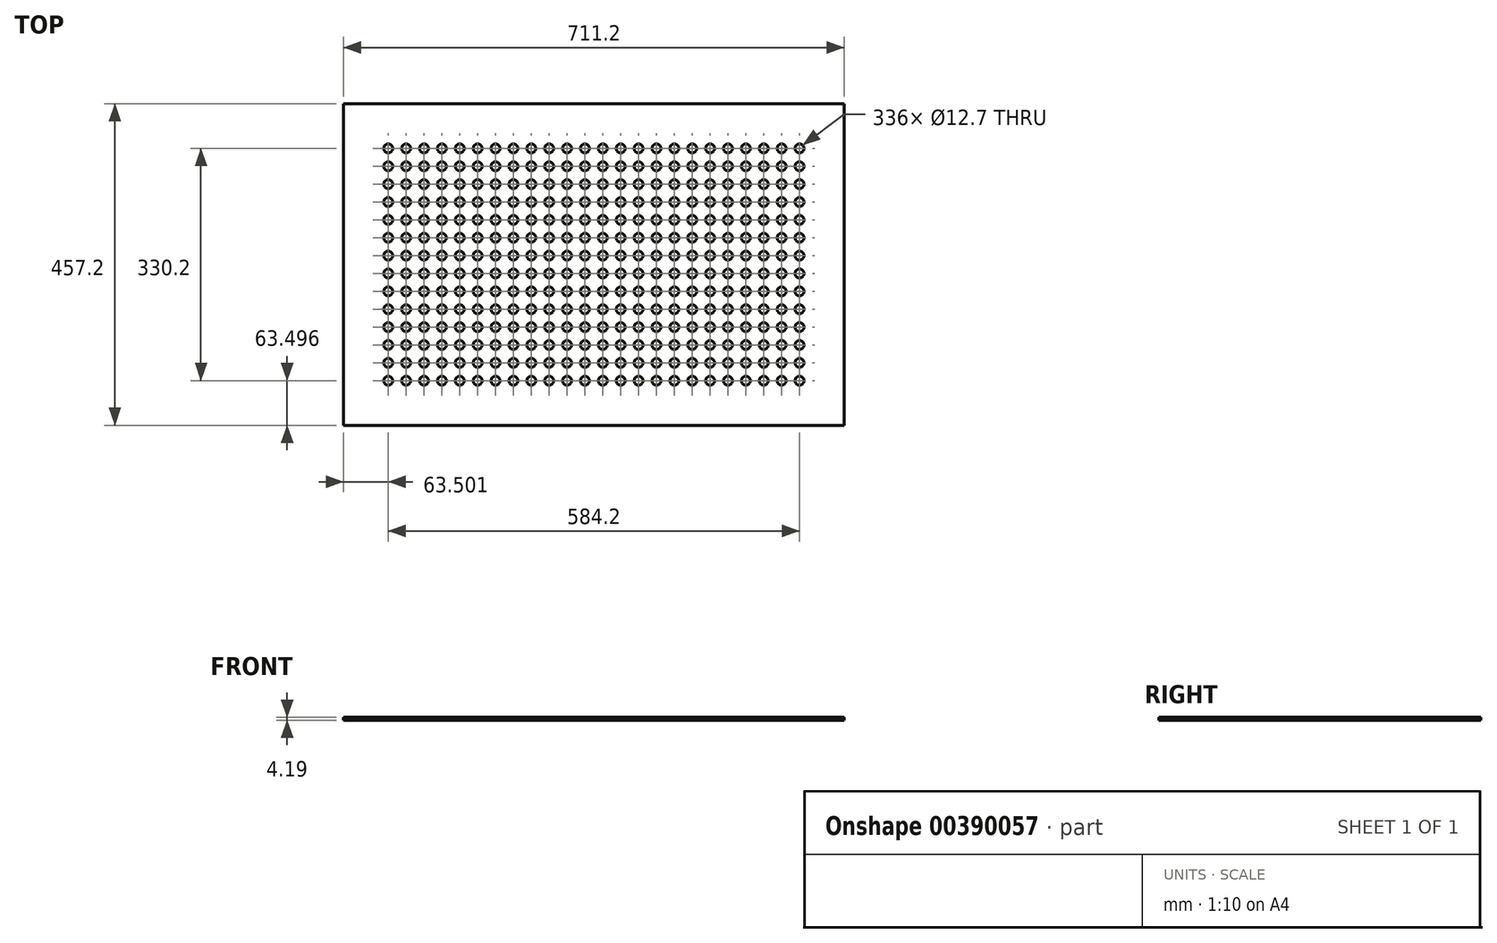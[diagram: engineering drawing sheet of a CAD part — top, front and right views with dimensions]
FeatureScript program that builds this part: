
annotation { "Feature Type Name" : "Feature", "Feature Type Description" : "" }
export const myFeature = defineFeature(function(context is Context, id is Id, definition is map)
    precondition{}
    {
        {
            var Q0;
            Q0=qCreatedBy(makeId("Top.planeOp"),FACE);
            var sketch = newSketch(context, id + "F0", { "sketchPlane" : qUnion([Q0])});
            skLineSegment(sketch, "E0.bottom", {"start": v(-350.77, 221.84) * mm, "end": v(360.43, 221.84) * mm});
            skLineSegment(sketch, "E0.top", {"start": v(-350.77, -235.36) * mm, "end": v(360.43, -235.36) * mm});
            skLineSegment(sketch, "E0.left", {"start": v(-350.77, 221.84) * mm, "end": v(-350.77, -235.36) * mm});
            skLineSegment(sketch, "E0.right", {"start": v(360.43, 221.84) * mm, "end": v(360.43, -235.36) * mm});
            skCircle(sketch, "E1", {"center": v(-287.27, 158.34) * mm, "radius": 6.35 * mm});
            skCircle(sketch, "E2.0.1.0", {"center": v(-287.27, 132.94) * mm, "radius": 6.35 * mm});
            skCircle(sketch, "E2.0.2.0", {"center": v(-287.27, 107.54) * mm, "radius": 6.35 * mm});
            skCircle(sketch, "E2.0.3.0", {"center": v(-287.27, 82.14) * mm, "radius": 6.35 * mm});
            skCircle(sketch, "E2.0.4.0", {"center": v(-287.27, 56.74) * mm, "radius": 6.35 * mm});
            skCircle(sketch, "E2.0.5.0", {"center": v(-287.27, 31.34) * mm, "radius": 6.35 * mm});
            skCircle(sketch, "E2.0.6.0", {"center": v(-287.27, 5.94) * mm, "radius": 6.35 * mm});
            skCircle(sketch, "E2.1.0.0", {"center": v(-261.87, 158.34) * mm, "radius": 6.35 * mm});
            skCircle(sketch, "E2.1.1.0", {"center": v(-261.87, 132.94) * mm, "radius": 6.35 * mm});
            skCircle(sketch, "E2.1.2.0", {"center": v(-261.87, 107.54) * mm, "radius": 6.35 * mm});
            skCircle(sketch, "E2.1.3.0", {"center": v(-261.87, 82.14) * mm, "radius": 6.35 * mm});
            skCircle(sketch, "E2.1.4.0", {"center": v(-261.87, 56.74) * mm, "radius": 6.35 * mm});
            skCircle(sketch, "E2.1.5.0", {"center": v(-261.87, 31.34) * mm, "radius": 6.35 * mm});
            skCircle(sketch, "E2.1.6.0", {"center": v(-261.87, 5.94) * mm, "radius": 6.35 * mm});
            skCircle(sketch, "E2.2.0.0", {"center": v(-236.47, 158.34) * mm, "radius": 6.35 * mm});
            skCircle(sketch, "E2.2.1.0", {"center": v(-236.47, 132.94) * mm, "radius": 6.35 * mm});
            skCircle(sketch, "E2.2.2.0", {"center": v(-236.47, 107.54) * mm, "radius": 6.35 * mm});
            skCircle(sketch, "E2.2.3.0", {"center": v(-236.47, 82.14) * mm, "radius": 6.35 * mm});
            skCircle(sketch, "E2.2.4.0", {"center": v(-236.47, 56.74) * mm, "radius": 6.35 * mm});
            skCircle(sketch, "E2.2.5.0", {"center": v(-236.47, 31.34) * mm, "radius": 6.35 * mm});
            skCircle(sketch, "E2.2.6.0", {"center": v(-236.47, 5.94) * mm, "radius": 6.35 * mm});
            skCircle(sketch, "E2.3.0.0", {"center": v(-211.07, 158.34) * mm, "radius": 6.35 * mm});
            skCircle(sketch, "E2.3.1.0", {"center": v(-211.07, 132.94) * mm, "radius": 6.35 * mm});
            skCircle(sketch, "E2.3.2.0", {"center": v(-211.07, 107.54) * mm, "radius": 6.35 * mm});
            skCircle(sketch, "E2.3.3.0", {"center": v(-211.07, 82.14) * mm, "radius": 6.35 * mm});
            skCircle(sketch, "E2.3.4.0", {"center": v(-211.07, 56.74) * mm, "radius": 6.35 * mm});
            skCircle(sketch, "E2.3.5.0", {"center": v(-211.07, 31.34) * mm, "radius": 6.35 * mm});
            skCircle(sketch, "E2.3.6.0", {"center": v(-211.07, 5.94) * mm, "radius": 6.35 * mm});
            skCircle(sketch, "E2.4.0.0", {"center": v(-185.67, 158.34) * mm, "radius": 6.35 * mm});
            skCircle(sketch, "E2.4.1.0", {"center": v(-185.67, 132.94) * mm, "radius": 6.35 * mm});
            skCircle(sketch, "E2.4.2.0", {"center": v(-185.67, 107.54) * mm, "radius": 6.35 * mm});
            skCircle(sketch, "E2.4.3.0", {"center": v(-185.67, 82.14) * mm, "radius": 6.35 * mm});
            skCircle(sketch, "E2.4.4.0", {"center": v(-185.67, 56.74) * mm, "radius": 6.35 * mm});
            skCircle(sketch, "E2.4.5.0", {"center": v(-185.67, 31.34) * mm, "radius": 6.35 * mm});
            skCircle(sketch, "E2.4.6.0", {"center": v(-185.67, 5.94) * mm, "radius": 6.35 * mm});
            skCircle(sketch, "E2.5.0.0", {"center": v(-160.27, 158.34) * mm, "radius": 6.35 * mm});
            skCircle(sketch, "E2.5.1.0", {"center": v(-160.27, 132.94) * mm, "radius": 6.35 * mm});
            skCircle(sketch, "E2.5.2.0", {"center": v(-160.27, 107.54) * mm, "radius": 6.35 * mm});
            skCircle(sketch, "E2.5.3.0", {"center": v(-160.27, 82.14) * mm, "radius": 6.35 * mm});
            skCircle(sketch, "E2.5.4.0", {"center": v(-160.27, 56.74) * mm, "radius": 6.35 * mm});
            skCircle(sketch, "E2.5.5.0", {"center": v(-160.27, 31.34) * mm, "radius": 6.35 * mm});
            skCircle(sketch, "E2.5.6.0", {"center": v(-160.27, 5.94) * mm, "radius": 6.35 * mm});
            skCircle(sketch, "E2.6.0.0", {"center": v(-134.87, 158.34) * mm, "radius": 6.35 * mm});
            skCircle(sketch, "E2.6.1.0", {"center": v(-134.87, 132.94) * mm, "radius": 6.35 * mm});
            skCircle(sketch, "E2.6.2.0", {"center": v(-134.87, 107.54) * mm, "radius": 6.35 * mm});
            skCircle(sketch, "E2.6.3.0", {"center": v(-134.87, 82.14) * mm, "radius": 6.35 * mm});
            skCircle(sketch, "E2.6.4.0", {"center": v(-134.87, 56.74) * mm, "radius": 6.35 * mm});
            skCircle(sketch, "E2.6.5.0", {"center": v(-134.87, 31.34) * mm, "radius": 6.35 * mm});
            skCircle(sketch, "E2.6.6.0", {"center": v(-134.87, 5.94) * mm, "radius": 6.35 * mm});
            skCircle(sketch, "E2.7.0.0", {"center": v(-109.47, 158.34) * mm, "radius": 6.35 * mm});
            skCircle(sketch, "E2.7.1.0", {"center": v(-109.47, 132.94) * mm, "radius": 6.35 * mm});
            skCircle(sketch, "E2.7.2.0", {"center": v(-109.47, 107.54) * mm, "radius": 6.35 * mm});
            skCircle(sketch, "E2.7.3.0", {"center": v(-109.47, 82.14) * mm, "radius": 6.35 * mm});
            skCircle(sketch, "E2.7.4.0", {"center": v(-109.47, 56.74) * mm, "radius": 6.35 * mm});
            skCircle(sketch, "E2.7.5.0", {"center": v(-109.47, 31.34) * mm, "radius": 6.35 * mm});
            skCircle(sketch, "E2.7.6.0", {"center": v(-109.47, 5.94) * mm, "radius": 6.35 * mm});
            skCircle(sketch, "E2.8.0.0", {"center": v(-84.07, 158.34) * mm, "radius": 6.35 * mm});
            skCircle(sketch, "E2.8.1.0", {"center": v(-84.07, 132.94) * mm, "radius": 6.35 * mm});
            skCircle(sketch, "E2.8.2.0", {"center": v(-84.07, 107.54) * mm, "radius": 6.35 * mm});
            skCircle(sketch, "E2.8.3.0", {"center": v(-84.07, 82.14) * mm, "radius": 6.35 * mm});
            skCircle(sketch, "E2.8.4.0", {"center": v(-84.07, 56.74) * mm, "radius": 6.35 * mm});
            skCircle(sketch, "E2.8.5.0", {"center": v(-84.07, 31.34) * mm, "radius": 6.35 * mm});
            skCircle(sketch, "E2.8.6.0", {"center": v(-84.07, 5.94) * mm, "radius": 6.35 * mm});
            skCircle(sketch, "E2.9.0.0", {"center": v(-58.67, 158.34) * mm, "radius": 6.35 * mm});
            skCircle(sketch, "E2.9.1.0", {"center": v(-58.67, 132.94) * mm, "radius": 6.35 * mm});
            skCircle(sketch, "E2.9.2.0", {"center": v(-58.67, 107.54) * mm, "radius": 6.35 * mm});
            skCircle(sketch, "E2.9.3.0", {"center": v(-58.67, 82.14) * mm, "radius": 6.35 * mm});
            skCircle(sketch, "E2.9.4.0", {"center": v(-58.67, 56.74) * mm, "radius": 6.35 * mm});
            skCircle(sketch, "E2.9.5.0", {"center": v(-58.67, 31.34) * mm, "radius": 6.35 * mm});
            skCircle(sketch, "E2.9.6.0", {"center": v(-58.67, 5.94) * mm, "radius": 6.35 * mm});
            skCircle(sketch, "E2.10.0.0", {"center": v(-33.27, 158.34) * mm, "radius": 6.35 * mm});
            skCircle(sketch, "E2.10.1.0", {"center": v(-33.27, 132.94) * mm, "radius": 6.35 * mm});
            skCircle(sketch, "E2.10.2.0", {"center": v(-33.27, 107.54) * mm, "radius": 6.35 * mm});
            skCircle(sketch, "E2.10.3.0", {"center": v(-33.27, 82.14) * mm, "radius": 6.35 * mm});
            skCircle(sketch, "E2.10.4.0", {"center": v(-33.27, 56.74) * mm, "radius": 6.35 * mm});
            skCircle(sketch, "E2.10.5.0", {"center": v(-33.27, 31.34) * mm, "radius": 6.35 * mm});
            skCircle(sketch, "E2.10.6.0", {"center": v(-33.27, 5.94) * mm, "radius": 6.35 * mm});
            skCircle(sketch, "E2.11.0.0", {"center": v(-7.87, 158.34) * mm, "radius": 6.35 * mm});
            skCircle(sketch, "E2.11.1.0", {"center": v(-7.87, 132.94) * mm, "radius": 6.35 * mm});
            skCircle(sketch, "E2.11.2.0", {"center": v(-7.87, 107.54) * mm, "radius": 6.35 * mm});
            skCircle(sketch, "E2.11.3.0", {"center": v(-7.87, 82.14) * mm, "radius": 6.35 * mm});
            skCircle(sketch, "E2.11.4.0", {"center": v(-7.87, 56.74) * mm, "radius": 6.35 * mm});
            skCircle(sketch, "E2.11.5.0", {"center": v(-7.87, 31.34) * mm, "radius": 6.35 * mm});
            skCircle(sketch, "E2.11.6.0", {"center": v(-7.87, 5.94) * mm, "radius": 6.35 * mm});
            skLineSegment(sketch, "E2.direction1", {"start": v(-287.27, 158.34) * mm, "end": v(-261.87, 158.34) * mm, "construction": true});
            skLineSegment(sketch, "E2.direction2", {"start": v(-287.27, 158.34) * mm, "end": v(-287.27, 132.94) * mm, "construction": true});
            skCircle(sketch, "E3.0.12.0", {"center": v(17.53, 158.34) * mm, "radius": 6.35 * mm});
            skCircle(sketch, "E3.0.12.1", {"center": v(17.53, 132.94) * mm, "radius": 6.35 * mm});
            skCircle(sketch, "E3.0.12.2", {"center": v(17.53, 107.54) * mm, "radius": 6.35 * mm});
            skCircle(sketch, "E3.0.12.3", {"center": v(17.53, 82.14) * mm, "radius": 6.35 * mm});
            skCircle(sketch, "E3.0.12.4", {"center": v(17.53, 56.74) * mm, "radius": 6.35 * mm});
            skCircle(sketch, "E3.0.12.5", {"center": v(17.53, 31.34) * mm, "radius": 6.35 * mm});
            skCircle(sketch, "E3.0.12.6", {"center": v(17.53, 5.94) * mm, "radius": 6.35 * mm});
            skCircle(sketch, "E3.0.13.0", {"center": v(42.93, 158.34) * mm, "radius": 6.35 * mm});
            skCircle(sketch, "E3.0.13.1", {"center": v(42.93, 132.94) * mm, "radius": 6.35 * mm});
            skCircle(sketch, "E3.0.13.2", {"center": v(42.93, 107.54) * mm, "radius": 6.35 * mm});
            skCircle(sketch, "E3.0.13.3", {"center": v(42.93, 82.14) * mm, "radius": 6.35 * mm});
            skCircle(sketch, "E3.0.13.4", {"center": v(42.93, 56.74) * mm, "radius": 6.35 * mm});
            skCircle(sketch, "E3.0.13.5", {"center": v(42.93, 31.34) * mm, "radius": 6.35 * mm});
            skCircle(sketch, "E3.0.13.6", {"center": v(42.93, 5.94) * mm, "radius": 6.35 * mm});
            skCircle(sketch, "E3.0.14.0", {"center": v(68.33, 158.34) * mm, "radius": 6.35 * mm});
            skCircle(sketch, "E3.0.14.1", {"center": v(68.33, 132.94) * mm, "radius": 6.35 * mm});
            skCircle(sketch, "E3.0.14.2", {"center": v(68.33, 107.54) * mm, "radius": 6.35 * mm});
            skCircle(sketch, "E3.0.14.3", {"center": v(68.33, 82.14) * mm, "radius": 6.35 * mm});
            skCircle(sketch, "E3.0.14.4", {"center": v(68.33, 56.74) * mm, "radius": 6.35 * mm});
            skCircle(sketch, "E3.0.14.5", {"center": v(68.33, 31.34) * mm, "radius": 6.35 * mm});
            skCircle(sketch, "E3.0.14.6", {"center": v(68.33, 5.94) * mm, "radius": 6.35 * mm});
            skCircle(sketch, "E3.0.15.0", {"center": v(93.73, 158.34) * mm, "radius": 6.35 * mm});
            skCircle(sketch, "E3.0.15.1", {"center": v(93.73, 132.94) * mm, "radius": 6.35 * mm});
            skCircle(sketch, "E3.0.15.2", {"center": v(93.73, 107.54) * mm, "radius": 6.35 * mm});
            skCircle(sketch, "E3.0.15.3", {"center": v(93.73, 82.14) * mm, "radius": 6.35 * mm});
            skCircle(sketch, "E3.0.15.4", {"center": v(93.73, 56.74) * mm, "radius": 6.35 * mm});
            skCircle(sketch, "E3.0.15.5", {"center": v(93.73, 31.34) * mm, "radius": 6.35 * mm});
            skCircle(sketch, "E3.0.15.6", {"center": v(93.73, 5.94) * mm, "radius": 6.35 * mm});
            skCircle(sketch, "E3.0.16.0", {"center": v(119.13, 158.34) * mm, "radius": 6.35 * mm});
            skCircle(sketch, "E3.0.16.1", {"center": v(119.13, 132.94) * mm, "radius": 6.35 * mm});
            skCircle(sketch, "E3.0.16.2", {"center": v(119.13, 107.54) * mm, "radius": 6.35 * mm});
            skCircle(sketch, "E3.0.16.3", {"center": v(119.13, 82.14) * mm, "radius": 6.35 * mm});
            skCircle(sketch, "E3.0.16.4", {"center": v(119.13, 56.74) * mm, "radius": 6.35 * mm});
            skCircle(sketch, "E3.0.16.5", {"center": v(119.13, 31.34) * mm, "radius": 6.35 * mm});
            skCircle(sketch, "E3.0.16.6", {"center": v(119.13, 5.94) * mm, "radius": 6.35 * mm});
            skCircle(sketch, "E3.0.17.0", {"center": v(144.53, 158.34) * mm, "radius": 6.35 * mm});
            skCircle(sketch, "E3.0.17.1", {"center": v(144.53, 132.94) * mm, "radius": 6.35 * mm});
            skCircle(sketch, "E3.0.17.2", {"center": v(144.53, 107.54) * mm, "radius": 6.35 * mm});
            skCircle(sketch, "E3.0.17.3", {"center": v(144.53, 82.14) * mm, "radius": 6.35 * mm});
            skCircle(sketch, "E3.0.17.4", {"center": v(144.53, 56.74) * mm, "radius": 6.35 * mm});
            skCircle(sketch, "E3.0.17.5", {"center": v(144.53, 31.34) * mm, "radius": 6.35 * mm});
            skCircle(sketch, "E3.0.17.6", {"center": v(144.53, 5.94) * mm, "radius": 6.35 * mm});
            skCircle(sketch, "E3.0.18.0", {"center": v(169.93, 158.34) * mm, "radius": 6.35 * mm});
            skCircle(sketch, "E3.0.18.1", {"center": v(169.93, 132.94) * mm, "radius": 6.35 * mm});
            skCircle(sketch, "E3.0.18.2", {"center": v(169.93, 107.54) * mm, "radius": 6.35 * mm});
            skCircle(sketch, "E3.0.18.3", {"center": v(169.93, 82.14) * mm, "radius": 6.35 * mm});
            skCircle(sketch, "E3.0.18.4", {"center": v(169.93, 56.74) * mm, "radius": 6.35 * mm});
            skCircle(sketch, "E3.0.18.5", {"center": v(169.93, 31.34) * mm, "radius": 6.35 * mm});
            skCircle(sketch, "E3.0.18.6", {"center": v(169.93, 5.94) * mm, "radius": 6.35 * mm});
            skCircle(sketch, "E3.0.19.0", {"center": v(195.33, 158.34) * mm, "radius": 6.35 * mm});
            skCircle(sketch, "E3.0.19.1", {"center": v(195.33, 132.94) * mm, "radius": 6.35 * mm});
            skCircle(sketch, "E3.0.19.2", {"center": v(195.33, 107.54) * mm, "radius": 6.35 * mm});
            skCircle(sketch, "E3.0.19.3", {"center": v(195.33, 82.14) * mm, "radius": 6.35 * mm});
            skCircle(sketch, "E3.0.19.4", {"center": v(195.33, 56.74) * mm, "radius": 6.35 * mm});
            skCircle(sketch, "E3.0.19.5", {"center": v(195.33, 31.34) * mm, "radius": 6.35 * mm});
            skCircle(sketch, "E3.0.19.6", {"center": v(195.33, 5.94) * mm, "radius": 6.35 * mm});
            skCircle(sketch, "E4.0.20.0", {"center": v(220.73, 158.34) * mm, "radius": 6.35 * mm});
            skCircle(sketch, "E4.0.20.1", {"center": v(220.73, 132.94) * mm, "radius": 6.35 * mm});
            skCircle(sketch, "E4.0.20.2", {"center": v(220.73, 107.54) * mm, "radius": 6.35 * mm});
            skCircle(sketch, "E4.0.20.3", {"center": v(220.73, 82.14) * mm, "radius": 6.35 * mm});
            skCircle(sketch, "E4.0.20.4", {"center": v(220.73, 56.74) * mm, "radius": 6.35 * mm});
            skCircle(sketch, "E4.0.20.5", {"center": v(220.73, 31.34) * mm, "radius": 6.35 * mm});
            skCircle(sketch, "E4.0.20.6", {"center": v(220.73, 5.94) * mm, "radius": 6.35 * mm});
            skCircle(sketch, "E4.0.21.0", {"center": v(246.13, 158.34) * mm, "radius": 6.35 * mm});
            skCircle(sketch, "E4.0.21.1", {"center": v(246.13, 132.94) * mm, "radius": 6.35 * mm});
            skCircle(sketch, "E4.0.21.2", {"center": v(246.13, 107.54) * mm, "radius": 6.35 * mm});
            skCircle(sketch, "E4.0.21.3", {"center": v(246.13, 82.14) * mm, "radius": 6.35 * mm});
            skCircle(sketch, "E4.0.21.4", {"center": v(246.13, 56.74) * mm, "radius": 6.35 * mm});
            skCircle(sketch, "E4.0.21.5", {"center": v(246.13, 31.34) * mm, "radius": 6.35 * mm});
            skCircle(sketch, "E4.0.21.6", {"center": v(246.13, 5.94) * mm, "radius": 6.35 * mm});
            skCircle(sketch, "E4.0.22.0", {"center": v(271.53, 158.34) * mm, "radius": 6.35 * mm});
            skCircle(sketch, "E4.0.22.1", {"center": v(271.53, 132.94) * mm, "radius": 6.35 * mm});
            skCircle(sketch, "E4.0.22.2", {"center": v(271.53, 107.54) * mm, "radius": 6.35 * mm});
            skCircle(sketch, "E4.0.22.3", {"center": v(271.53, 82.14) * mm, "radius": 6.35 * mm});
            skCircle(sketch, "E4.0.22.4", {"center": v(271.53, 56.74) * mm, "radius": 6.35 * mm});
            skCircle(sketch, "E4.0.22.5", {"center": v(271.53, 31.34) * mm, "radius": 6.35 * mm});
            skCircle(sketch, "E4.0.22.6", {"center": v(271.53, 5.94) * mm, "radius": 6.35 * mm});
            skCircle(sketch, "E4.0.23.0", {"center": v(296.93, 158.34) * mm, "radius": 6.35 * mm});
            skCircle(sketch, "E4.0.23.1", {"center": v(296.93, 132.94) * mm, "radius": 6.35 * mm});
            skCircle(sketch, "E4.0.23.2", {"center": v(296.93, 107.54) * mm, "radius": 6.35 * mm});
            skCircle(sketch, "E4.0.23.3", {"center": v(296.93, 82.14) * mm, "radius": 6.35 * mm});
            skCircle(sketch, "E4.0.23.4", {"center": v(296.93, 56.74) * mm, "radius": 6.35 * mm});
            skCircle(sketch, "E4.0.23.5", {"center": v(296.93, 31.34) * mm, "radius": 6.35 * mm});
            skCircle(sketch, "E4.0.23.6", {"center": v(296.93, 5.94) * mm, "radius": 6.35 * mm});
            skCircle(sketch, "E5.0.0.7", {"center": v(-287.27, -19.46) * mm, "radius": 6.35 * mm});
            skCircle(sketch, "E5.0.0.8", {"center": v(-287.27, -44.86) * mm, "radius": 6.35 * mm});
            skCircle(sketch, "E5.0.0.9", {"center": v(-287.27, -70.26) * mm, "radius": 6.35 * mm});
            skCircle(sketch, "E5.0.0.10", {"center": v(-287.27, -95.66) * mm, "radius": 6.35 * mm});
            skCircle(sketch, "E5.0.0.11", {"center": v(-287.27, -121.06) * mm, "radius": 6.35 * mm});
            skCircle(sketch, "E5.0.0.12", {"center": v(-287.27, -146.46) * mm, "radius": 6.35 * mm});
            skCircle(sketch, "E5.0.0.13", {"center": v(-287.27, -171.86) * mm, "radius": 6.35 * mm});
            skCircle(sketch, "E5.0.1.7", {"center": v(-261.87, -19.46) * mm, "radius": 6.35 * mm});
            skCircle(sketch, "E5.0.1.8", {"center": v(-261.87, -44.86) * mm, "radius": 6.35 * mm});
            skCircle(sketch, "E5.0.1.9", {"center": v(-261.87, -70.26) * mm, "radius": 6.35 * mm});
            skCircle(sketch, "E5.0.1.10", {"center": v(-261.87, -95.66) * mm, "radius": 6.35 * mm});
            skCircle(sketch, "E5.0.1.11", {"center": v(-261.87, -121.06) * mm, "radius": 6.35 * mm});
            skCircle(sketch, "E5.0.1.12", {"center": v(-261.87, -146.46) * mm, "radius": 6.35 * mm});
            skCircle(sketch, "E5.0.1.13", {"center": v(-261.87, -171.86) * mm, "radius": 6.35 * mm});
            skCircle(sketch, "E5.0.2.7", {"center": v(-236.47, -19.46) * mm, "radius": 6.35 * mm});
            skCircle(sketch, "E5.0.2.8", {"center": v(-236.47, -44.86) * mm, "radius": 6.35 * mm});
            skCircle(sketch, "E5.0.2.9", {"center": v(-236.47, -70.26) * mm, "radius": 6.35 * mm});
            skCircle(sketch, "E5.0.2.10", {"center": v(-236.47, -95.66) * mm, "radius": 6.35 * mm});
            skCircle(sketch, "E5.0.2.11", {"center": v(-236.47, -121.06) * mm, "radius": 6.35 * mm});
            skCircle(sketch, "E5.0.2.12", {"center": v(-236.47, -146.46) * mm, "radius": 6.35 * mm});
            skCircle(sketch, "E5.0.2.13", {"center": v(-236.47, -171.86) * mm, "radius": 6.35 * mm});
            skCircle(sketch, "E5.0.3.7", {"center": v(-211.07, -19.46) * mm, "radius": 6.35 * mm});
            skCircle(sketch, "E5.0.3.8", {"center": v(-211.07, -44.86) * mm, "radius": 6.35 * mm});
            skCircle(sketch, "E5.0.3.9", {"center": v(-211.07, -70.26) * mm, "radius": 6.35 * mm});
            skCircle(sketch, "E5.0.3.10", {"center": v(-211.07, -95.66) * mm, "radius": 6.35 * mm});
            skCircle(sketch, "E5.0.3.11", {"center": v(-211.07, -121.06) * mm, "radius": 6.35 * mm});
            skCircle(sketch, "E5.0.3.12", {"center": v(-211.07, -146.46) * mm, "radius": 6.35 * mm});
            skCircle(sketch, "E5.0.3.13", {"center": v(-211.07, -171.86) * mm, "radius": 6.35 * mm});
            skCircle(sketch, "E5.0.4.7", {"center": v(-185.67, -19.46) * mm, "radius": 6.35 * mm});
            skCircle(sketch, "E5.0.4.8", {"center": v(-185.67, -44.86) * mm, "radius": 6.35 * mm});
            skCircle(sketch, "E5.0.4.9", {"center": v(-185.67, -70.26) * mm, "radius": 6.35 * mm});
            skCircle(sketch, "E5.0.4.10", {"center": v(-185.67, -95.66) * mm, "radius": 6.35 * mm});
            skCircle(sketch, "E5.0.4.11", {"center": v(-185.67, -121.06) * mm, "radius": 6.35 * mm});
            skCircle(sketch, "E5.0.4.12", {"center": v(-185.67, -146.46) * mm, "radius": 6.35 * mm});
            skCircle(sketch, "E5.0.4.13", {"center": v(-185.67, -171.86) * mm, "radius": 6.35 * mm});
            skCircle(sketch, "E5.0.5.7", {"center": v(-160.27, -19.46) * mm, "radius": 6.35 * mm});
            skCircle(sketch, "E5.0.5.8", {"center": v(-160.27, -44.86) * mm, "radius": 6.35 * mm});
            skCircle(sketch, "E5.0.5.9", {"center": v(-160.27, -70.26) * mm, "radius": 6.35 * mm});
            skCircle(sketch, "E5.0.5.10", {"center": v(-160.27, -95.66) * mm, "radius": 6.35 * mm});
            skCircle(sketch, "E5.0.5.11", {"center": v(-160.27, -121.06) * mm, "radius": 6.35 * mm});
            skCircle(sketch, "E5.0.5.12", {"center": v(-160.27, -146.46) * mm, "radius": 6.35 * mm});
            skCircle(sketch, "E5.0.5.13", {"center": v(-160.27, -171.86) * mm, "radius": 6.35 * mm});
            skCircle(sketch, "E5.0.6.7", {"center": v(-134.87, -19.46) * mm, "radius": 6.35 * mm});
            skCircle(sketch, "E5.0.6.8", {"center": v(-134.87, -44.86) * mm, "radius": 6.35 * mm});
            skCircle(sketch, "E5.0.6.9", {"center": v(-134.87, -70.26) * mm, "radius": 6.35 * mm});
            skCircle(sketch, "E5.0.6.10", {"center": v(-134.87, -95.66) * mm, "radius": 6.35 * mm});
            skCircle(sketch, "E5.0.6.11", {"center": v(-134.87, -121.06) * mm, "radius": 6.35 * mm});
            skCircle(sketch, "E5.0.6.12", {"center": v(-134.87, -146.46) * mm, "radius": 6.35 * mm});
            skCircle(sketch, "E5.0.6.13", {"center": v(-134.87, -171.86) * mm, "radius": 6.35 * mm});
            skCircle(sketch, "E5.0.7.7", {"center": v(-109.47, -19.46) * mm, "radius": 6.35 * mm});
            skCircle(sketch, "E5.0.7.8", {"center": v(-109.47, -44.86) * mm, "radius": 6.35 * mm});
            skCircle(sketch, "E5.0.7.9", {"center": v(-109.47, -70.26) * mm, "radius": 6.35 * mm});
            skCircle(sketch, "E5.0.7.10", {"center": v(-109.47, -95.66) * mm, "radius": 6.35 * mm});
            skCircle(sketch, "E5.0.7.11", {"center": v(-109.47, -121.06) * mm, "radius": 6.35 * mm});
            skCircle(sketch, "E5.0.7.12", {"center": v(-109.47, -146.46) * mm, "radius": 6.35 * mm});
            skCircle(sketch, "E5.0.7.13", {"center": v(-109.47, -171.86) * mm, "radius": 6.35 * mm});
            skCircle(sketch, "E5.0.8.7", {"center": v(-84.07, -19.46) * mm, "radius": 6.35 * mm});
            skCircle(sketch, "E5.0.8.8", {"center": v(-84.07, -44.86) * mm, "radius": 6.35 * mm});
            skCircle(sketch, "E5.0.8.9", {"center": v(-84.07, -70.26) * mm, "radius": 6.35 * mm});
            skCircle(sketch, "E5.0.8.10", {"center": v(-84.07, -95.66) * mm, "radius": 6.35 * mm});
            skCircle(sketch, "E5.0.8.11", {"center": v(-84.07, -121.06) * mm, "radius": 6.35 * mm});
            skCircle(sketch, "E5.0.8.12", {"center": v(-84.07, -146.46) * mm, "radius": 6.35 * mm});
            skCircle(sketch, "E5.0.8.13", {"center": v(-84.07, -171.86) * mm, "radius": 6.35 * mm});
            skCircle(sketch, "E5.0.9.7", {"center": v(-58.67, -19.46) * mm, "radius": 6.35 * mm});
            skCircle(sketch, "E5.0.9.8", {"center": v(-58.67, -44.86) * mm, "radius": 6.35 * mm});
            skCircle(sketch, "E5.0.9.9", {"center": v(-58.67, -70.26) * mm, "radius": 6.35 * mm});
            skCircle(sketch, "E5.0.9.10", {"center": v(-58.67, -95.66) * mm, "radius": 6.35 * mm});
            skCircle(sketch, "E5.0.9.11", {"center": v(-58.67, -121.06) * mm, "radius": 6.35 * mm});
            skCircle(sketch, "E5.0.9.12", {"center": v(-58.67, -146.46) * mm, "radius": 6.35 * mm});
            skCircle(sketch, "E5.0.9.13", {"center": v(-58.67, -171.86) * mm, "radius": 6.35 * mm});
            skCircle(sketch, "E5.0.10.7", {"center": v(-33.27, -19.46) * mm, "radius": 6.35 * mm});
            skCircle(sketch, "E5.0.10.8", {"center": v(-33.27, -44.86) * mm, "radius": 6.35 * mm});
            skCircle(sketch, "E5.0.10.9", {"center": v(-33.27, -70.26) * mm, "radius": 6.35 * mm});
            skCircle(sketch, "E5.0.10.10", {"center": v(-33.27, -95.66) * mm, "radius": 6.35 * mm});
            skCircle(sketch, "E5.0.10.11", {"center": v(-33.27, -121.06) * mm, "radius": 6.35 * mm});
            skCircle(sketch, "E5.0.10.12", {"center": v(-33.27, -146.46) * mm, "radius": 6.35 * mm});
            skCircle(sketch, "E5.0.10.13", {"center": v(-33.27, -171.86) * mm, "radius": 6.35 * mm});
            skCircle(sketch, "E5.0.11.7", {"center": v(-7.87, -19.46) * mm, "radius": 6.35 * mm});
            skCircle(sketch, "E5.0.11.8", {"center": v(-7.87, -44.86) * mm, "radius": 6.35 * mm});
            skCircle(sketch, "E5.0.11.9", {"center": v(-7.87, -70.26) * mm, "radius": 6.35 * mm});
            skCircle(sketch, "E5.0.11.10", {"center": v(-7.87, -95.66) * mm, "radius": 6.35 * mm});
            skCircle(sketch, "E5.0.11.11", {"center": v(-7.87, -121.06) * mm, "radius": 6.35 * mm});
            skCircle(sketch, "E5.0.11.12", {"center": v(-7.87, -146.46) * mm, "radius": 6.35 * mm});
            skCircle(sketch, "E5.0.11.13", {"center": v(-7.87, -171.86) * mm, "radius": 6.35 * mm});
            skCircle(sketch, "E5.0.12.7", {"center": v(17.53, -19.46) * mm, "radius": 6.35 * mm});
            skCircle(sketch, "E5.0.12.8", {"center": v(17.53, -44.86) * mm, "radius": 6.35 * mm});
            skCircle(sketch, "E5.0.12.9", {"center": v(17.53, -70.26) * mm, "radius": 6.35 * mm});
            skCircle(sketch, "E5.0.12.10", {"center": v(17.53, -95.66) * mm, "radius": 6.35 * mm});
            skCircle(sketch, "E5.0.12.11", {"center": v(17.53, -121.06) * mm, "radius": 6.35 * mm});
            skCircle(sketch, "E5.0.12.12", {"center": v(17.53, -146.46) * mm, "radius": 6.35 * mm});
            skCircle(sketch, "E5.0.12.13", {"center": v(17.53, -171.86) * mm, "radius": 6.35 * mm});
            skCircle(sketch, "E5.0.13.7", {"center": v(42.93, -19.46) * mm, "radius": 6.35 * mm});
            skCircle(sketch, "E5.0.13.8", {"center": v(42.93, -44.86) * mm, "radius": 6.35 * mm});
            skCircle(sketch, "E5.0.13.9", {"center": v(42.93, -70.26) * mm, "radius": 6.35 * mm});
            skCircle(sketch, "E5.0.13.10", {"center": v(42.93, -95.66) * mm, "radius": 6.35 * mm});
            skCircle(sketch, "E5.0.13.11", {"center": v(42.93, -121.06) * mm, "radius": 6.35 * mm});
            skCircle(sketch, "E5.0.13.12", {"center": v(42.93, -146.46) * mm, "radius": 6.35 * mm});
            skCircle(sketch, "E5.0.13.13", {"center": v(42.93, -171.86) * mm, "radius": 6.35 * mm});
            skCircle(sketch, "E5.0.14.7", {"center": v(68.33, -19.46) * mm, "radius": 6.35 * mm});
            skCircle(sketch, "E5.0.14.8", {"center": v(68.33, -44.86) * mm, "radius": 6.35 * mm});
            skCircle(sketch, "E5.0.14.9", {"center": v(68.33, -70.26) * mm, "radius": 6.35 * mm});
            skCircle(sketch, "E5.0.14.10", {"center": v(68.33, -95.66) * mm, "radius": 6.35 * mm});
            skCircle(sketch, "E5.0.14.11", {"center": v(68.33, -121.06) * mm, "radius": 6.35 * mm});
            skCircle(sketch, "E5.0.14.12", {"center": v(68.33, -146.46) * mm, "radius": 6.35 * mm});
            skCircle(sketch, "E5.0.14.13", {"center": v(68.33, -171.86) * mm, "radius": 6.35 * mm});
            skCircle(sketch, "E5.0.15.7", {"center": v(93.73, -19.46) * mm, "radius": 6.35 * mm});
            skCircle(sketch, "E5.0.15.8", {"center": v(93.73, -44.86) * mm, "radius": 6.35 * mm});
            skCircle(sketch, "E5.0.15.9", {"center": v(93.73, -70.26) * mm, "radius": 6.35 * mm});
            skCircle(sketch, "E5.0.15.10", {"center": v(93.73, -95.66) * mm, "radius": 6.35 * mm});
            skCircle(sketch, "E5.0.15.11", {"center": v(93.73, -121.06) * mm, "radius": 6.35 * mm});
            skCircle(sketch, "E5.0.15.12", {"center": v(93.73, -146.46) * mm, "radius": 6.35 * mm});
            skCircle(sketch, "E5.0.15.13", {"center": v(93.73, -171.86) * mm, "radius": 6.35 * mm});
            skCircle(sketch, "E5.0.16.7", {"center": v(119.13, -19.46) * mm, "radius": 6.35 * mm});
            skCircle(sketch, "E5.0.16.8", {"center": v(119.13, -44.86) * mm, "radius": 6.35 * mm});
            skCircle(sketch, "E5.0.16.9", {"center": v(119.13, -70.26) * mm, "radius": 6.35 * mm});
            skCircle(sketch, "E5.0.16.10", {"center": v(119.13, -95.66) * mm, "radius": 6.35 * mm});
            skCircle(sketch, "E5.0.16.11", {"center": v(119.13, -121.06) * mm, "radius": 6.35 * mm});
            skCircle(sketch, "E5.0.16.12", {"center": v(119.13, -146.46) * mm, "radius": 6.35 * mm});
            skCircle(sketch, "E5.0.16.13", {"center": v(119.13, -171.86) * mm, "radius": 6.35 * mm});
            skCircle(sketch, "E5.0.17.7", {"center": v(144.53, -19.46) * mm, "radius": 6.35 * mm});
            skCircle(sketch, "E5.0.17.8", {"center": v(144.53, -44.86) * mm, "radius": 6.35 * mm});
            skCircle(sketch, "E5.0.17.9", {"center": v(144.53, -70.26) * mm, "radius": 6.35 * mm});
            skCircle(sketch, "E5.0.17.10", {"center": v(144.53, -95.66) * mm, "radius": 6.35 * mm});
            skCircle(sketch, "E5.0.17.11", {"center": v(144.53, -121.06) * mm, "radius": 6.35 * mm});
            skCircle(sketch, "E5.0.17.12", {"center": v(144.53, -146.46) * mm, "radius": 6.35 * mm});
            skCircle(sketch, "E5.0.17.13", {"center": v(144.53, -171.86) * mm, "radius": 6.35 * mm});
            skCircle(sketch, "E5.0.18.7", {"center": v(169.93, -19.46) * mm, "radius": 6.35 * mm});
            skCircle(sketch, "E5.0.18.8", {"center": v(169.93, -44.86) * mm, "radius": 6.35 * mm});
            skCircle(sketch, "E5.0.18.9", {"center": v(169.93, -70.26) * mm, "radius": 6.35 * mm});
            skCircle(sketch, "E5.0.18.10", {"center": v(169.93, -95.66) * mm, "radius": 6.35 * mm});
            skCircle(sketch, "E5.0.18.11", {"center": v(169.93, -121.06) * mm, "radius": 6.35 * mm});
            skCircle(sketch, "E5.0.18.12", {"center": v(169.93, -146.46) * mm, "radius": 6.35 * mm});
            skCircle(sketch, "E5.0.18.13", {"center": v(169.93, -171.86) * mm, "radius": 6.35 * mm});
            skCircle(sketch, "E5.0.19.7", {"center": v(195.33, -19.46) * mm, "radius": 6.35 * mm});
            skCircle(sketch, "E5.0.19.8", {"center": v(195.33, -44.86) * mm, "radius": 6.35 * mm});
            skCircle(sketch, "E5.0.19.9", {"center": v(195.33, -70.26) * mm, "radius": 6.35 * mm});
            skCircle(sketch, "E5.0.19.10", {"center": v(195.33, -95.66) * mm, "radius": 6.35 * mm});
            skCircle(sketch, "E5.0.19.11", {"center": v(195.33, -121.06) * mm, "radius": 6.35 * mm});
            skCircle(sketch, "E5.0.19.12", {"center": v(195.33, -146.46) * mm, "radius": 6.35 * mm});
            skCircle(sketch, "E5.0.19.13", {"center": v(195.33, -171.86) * mm, "radius": 6.35 * mm});
            skCircle(sketch, "E5.0.20.7", {"center": v(220.73, -19.46) * mm, "radius": 6.35 * mm});
            skCircle(sketch, "E5.0.20.8", {"center": v(220.73, -44.86) * mm, "radius": 6.35 * mm});
            skCircle(sketch, "E5.0.20.9", {"center": v(220.73, -70.26) * mm, "radius": 6.35 * mm});
            skCircle(sketch, "E5.0.20.10", {"center": v(220.73, -95.66) * mm, "radius": 6.35 * mm});
            skCircle(sketch, "E5.0.20.11", {"center": v(220.73, -121.06) * mm, "radius": 6.35 * mm});
            skCircle(sketch, "E5.0.20.12", {"center": v(220.73, -146.46) * mm, "radius": 6.35 * mm});
            skCircle(sketch, "E5.0.20.13", {"center": v(220.73, -171.86) * mm, "radius": 6.35 * mm});
            skCircle(sketch, "E5.0.21.7", {"center": v(246.13, -19.46) * mm, "radius": 6.35 * mm});
            skCircle(sketch, "E5.0.21.8", {"center": v(246.13, -44.86) * mm, "radius": 6.35 * mm});
            skCircle(sketch, "E5.0.21.9", {"center": v(246.13, -70.26) * mm, "radius": 6.35 * mm});
            skCircle(sketch, "E5.0.21.10", {"center": v(246.13, -95.66) * mm, "radius": 6.35 * mm});
            skCircle(sketch, "E5.0.21.11", {"center": v(246.13, -121.06) * mm, "radius": 6.35 * mm});
            skCircle(sketch, "E5.0.21.12", {"center": v(246.13, -146.46) * mm, "radius": 6.35 * mm});
            skCircle(sketch, "E5.0.21.13", {"center": v(246.13, -171.86) * mm, "radius": 6.35 * mm});
            skCircle(sketch, "E5.0.22.7", {"center": v(271.53, -19.46) * mm, "radius": 6.35 * mm});
            skCircle(sketch, "E5.0.22.8", {"center": v(271.53, -44.86) * mm, "radius": 6.35 * mm});
            skCircle(sketch, "E5.0.22.9", {"center": v(271.53, -70.26) * mm, "radius": 6.35 * mm});
            skCircle(sketch, "E5.0.22.10", {"center": v(271.53, -95.66) * mm, "radius": 6.35 * mm});
            skCircle(sketch, "E5.0.22.11", {"center": v(271.53, -121.06) * mm, "radius": 6.35 * mm});
            skCircle(sketch, "E5.0.22.12", {"center": v(271.53, -146.46) * mm, "radius": 6.35 * mm});
            skCircle(sketch, "E5.0.22.13", {"center": v(271.53, -171.86) * mm, "radius": 6.35 * mm});
            skCircle(sketch, "E5.0.23.7", {"center": v(296.93, -19.46) * mm, "radius": 6.35 * mm});
            skCircle(sketch, "E5.0.23.8", {"center": v(296.93, -44.86) * mm, "radius": 6.35 * mm});
            skCircle(sketch, "E5.0.23.9", {"center": v(296.93, -70.26) * mm, "radius": 6.35 * mm});
            skCircle(sketch, "E5.0.23.10", {"center": v(296.93, -95.66) * mm, "radius": 6.35 * mm});
            skCircle(sketch, "E5.0.23.11", {"center": v(296.93, -121.06) * mm, "radius": 6.35 * mm});
            skCircle(sketch, "E5.0.23.12", {"center": v(296.93, -146.46) * mm, "radius": 6.35 * mm});
            skCircle(sketch, "E5.0.23.13", {"center": v(296.93, -171.86) * mm, "radius": 6.35 * mm});
            skSolve(sketch);
        }
        {
            var Q0;
            Q0=makeQuery(id+"F0.imprint","IMPRINT",FACE,{"disambiguationData":[TD([[makeQuery(id+"F0.imprint","IMPRINT",EDGE,{"derivedFrom":sQuery(id+"F0.wireOp",EDGE,"E0.bottom")}),-1.0]])]});
            extrude(context, id + "F1", {"entities" : qUnion([Q0]), "depth" : 4.2 * mm});
        }
    });
